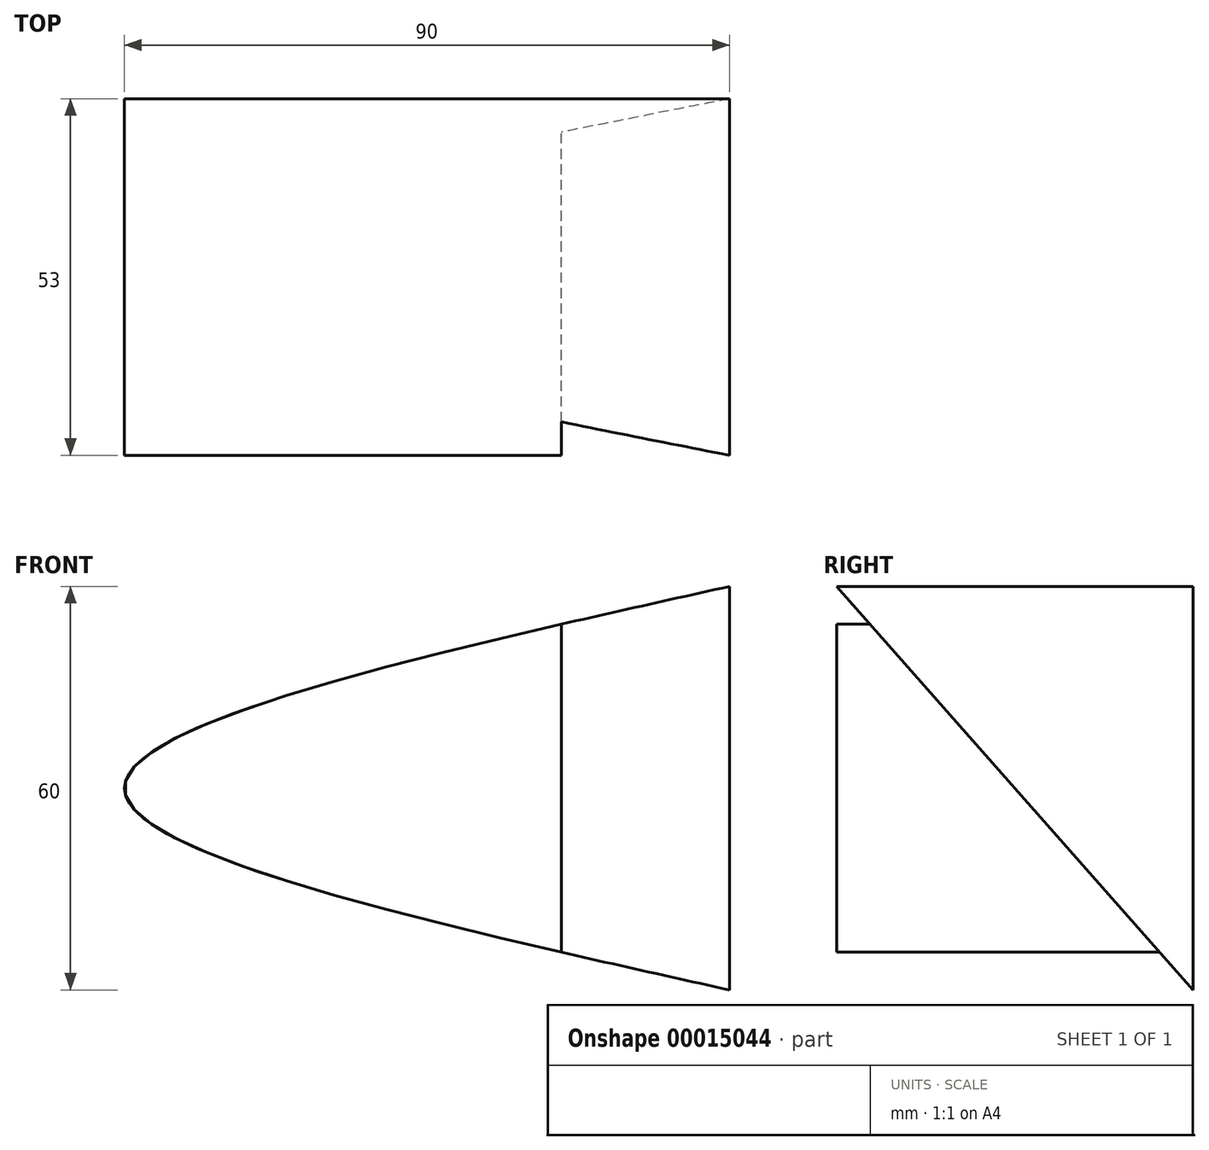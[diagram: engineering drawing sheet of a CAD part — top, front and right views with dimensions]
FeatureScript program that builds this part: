
annotation { "Feature Type Name" : "Feature", "Feature Type Description" : "" }
export const myFeature = defineFeature(function(context is Context, id is Id, definition is map)
    precondition{}
    {
        {
            var Q0;
            Q0=qCreatedBy(makeId("Front.planeOp"),FACE);
            var sketch = newSketch(context, id + "F0", { "sketchPlane" : qUnion([Q0])});
            skLineSegment(sketch, "E0.bottom", {"start": v(0, 0) * mm, "end": v(-110, 0) * mm});
            skLineSegment(sketch, "E0.top", {"start": v(0, 60) * mm, "end": v(-110, 60) * mm});
            skLineSegment(sketch, "E0.left", {"start": v(0, 0) * mm, "end": v(0, 60) * mm});
            skLineSegment(sketch, "E0.right", {"start": v(-110, 0) * mm, "end": v(-110, 60) * mm});
            skFitSpline(sketch, "E1", {"points": [v(0, 60) * mm, v(-90, 30) * mm, v(0, 0) * mm], "startDerivative": vector(-270, -60) * mm, "endDerivative": vector(270, -60) * mm});
            skSolve(sketch);
        }
        {
            var Q0;
            Q0=makeQuery(id+"F0.imprint","IMPRINT",FACE,{"disambiguationData":[TD([[makeQuery(id+"F0.imprint","IMPRINT",EDGE,{"derivedFrom":sQuery(id+"F0.wireOp",EDGE,"E0.left")}),1.0]])]});
            extrude(context, id + "F1", {"entities" : qUnion([Q0]), "depth" : 53 * mm});
        }
        {
            var Q0;
            Q0=makeQuery(id+"F1.opExtrude","SWEPT_FACE",FACE,{"disambiguationData":[OSD([sQuery(id+"F0.wireOp",EDGE,"E0.left")])]});
            var sketch = newSketch(context, id + "F2", { "sketchPlane" : qUnion([Q0])});
            skLineSegment(sketch, "E2", {"start": v(0, 60) * mm, "end": v(-53, 0) * mm});
            skLineSegment(sketch, "E3", {"start": v(0, 0) * mm, "end": v(-53, 60) * mm});
            skCircle(sketch, "E4", {"center": v(-26.5, 30) * mm, "radius": 3.75 * mm});
            skSolve(sketch);
        }
        {
            var Q0;
            {var subQ0=sQuery(id+"F2.wireOp",EDGE,"E4");var subQ3=sQuery(id+"F2.wireOp",EDGE,"E2");var subQ4=makeQuery(id+"F2.imprint","INTERSECT",VERTEX,{"disambiguationData":[OD(0.0)],"derivedFrom":[subQ3,subQ0]});Q0=makeQuery(id+"F2.imprint","IMPRINT",FACE,{"disambiguationData":[TD([[makeQuery(id+"F2.imprint","IMPRINT",EDGE,{"disambiguationData":[TD([[subQ4,-1.0]])],"derivedFrom":subQ3}),-1.0]])]});}
            var Q1;
            {var subQ1=sQuery(id+"F2.wireOp",EDGE,"E3");var subQ3=sQuery(id+"F2.wireOp",EDGE,"E2");var subQ5=makeQuery(id+"F2.imprint","INTERSECT",VERTEX,{"derivedFrom":[subQ3,subQ1]});Q1=makeQuery(id+"F2.imprint","IMPRINT",FACE,{"disambiguationData":[TD([[makeQuery(id+"F2.imprint","IMPRINT",EDGE,{"disambiguationData":[TD([[subQ5,-1.0]])],"derivedFrom":subQ3}),1.0]])]});}
            var Q2;
            {var subQ1=sQuery(id+"F2.wireOp",EDGE,"E3");var subQ3=sQuery(id+"F2.wireOp",EDGE,"E2");var subQ5=makeQuery(id+"F2.imprint","INTERSECT",VERTEX,{"derivedFrom":[subQ3,subQ1]});Q2=makeQuery(id+"F2.imprint","IMPRINT",FACE,{"disambiguationData":[TD([[makeQuery(id+"F2.imprint","IMPRINT",EDGE,{"disambiguationData":[TD([[subQ5,-1.0]])],"derivedFrom":subQ3}),-1.0]])]});}
            var Q3;
            {var subQ0=sQuery(id+"F2.wireOp",EDGE,"E4");var subQ3=sQuery(id+"F2.wireOp",EDGE,"E2");var subQ4=makeQuery(id+"F2.imprint","INTERSECT",VERTEX,{"disambiguationData":[OD(0.0)],"derivedFrom":[subQ3,subQ0]});Q3=makeQuery(id+"F2.imprint","IMPRINT",FACE,{"disambiguationData":[TD([[makeQuery(id+"F2.imprint","IMPRINT",EDGE,{"disambiguationData":[TD([[subQ4,-1.0]])],"derivedFrom":subQ3}),1.0]])]});}
            extrude(context, id + "F3", {"entities" : qUnion([Q0, Q1, Q2, Q3]), "operationType" : NewBodyOperationType.REMOVE, "oppositeDirection" : true, "depth" : 25 * mm});
        }
    });
